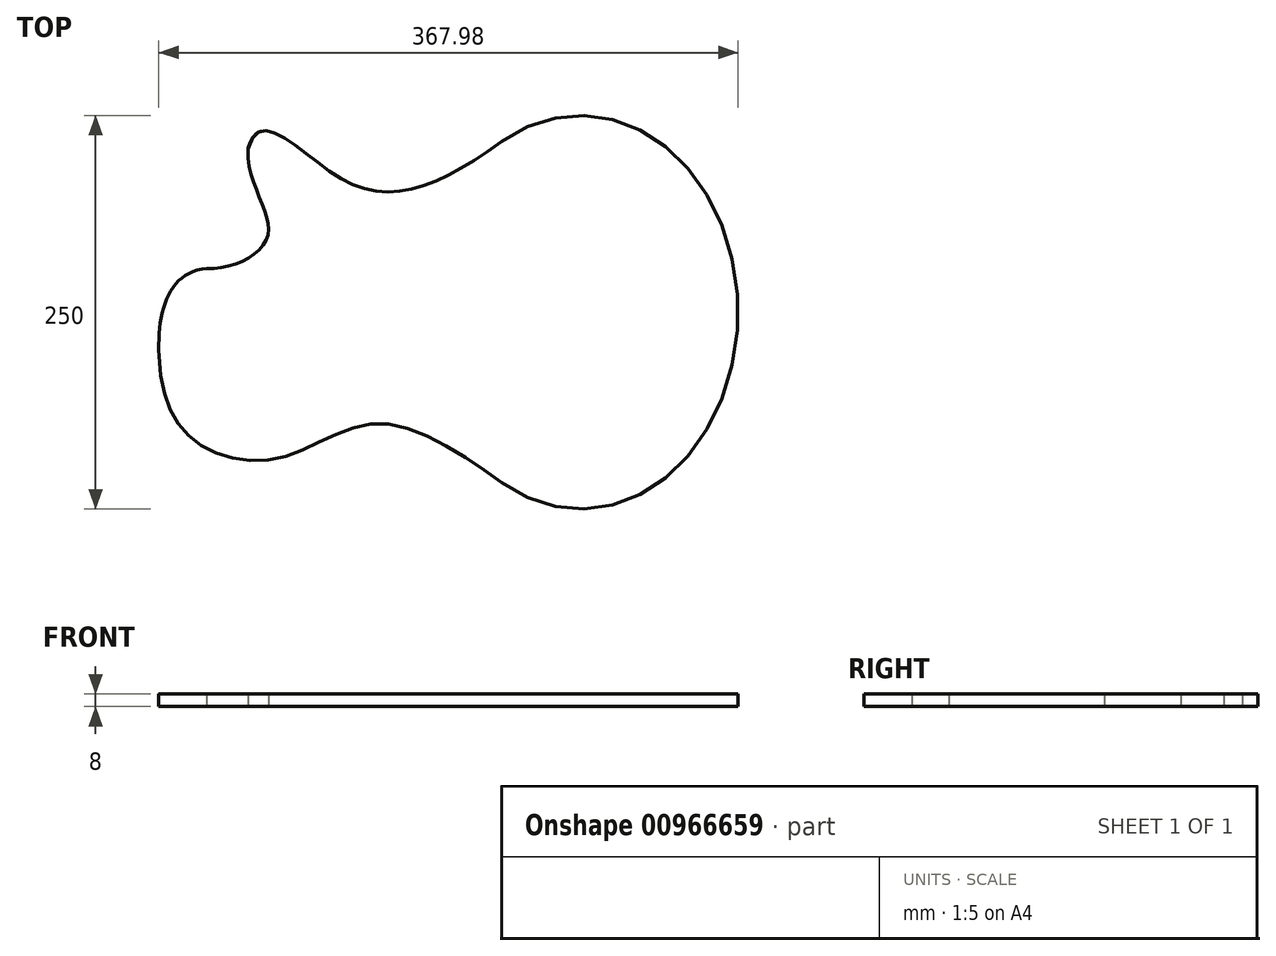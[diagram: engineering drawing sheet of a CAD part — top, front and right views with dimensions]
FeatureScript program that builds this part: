
annotation { "Feature Type Name" : "Feature", "Feature Type Description" : "" }
export const myFeature = defineFeature(function(context is Context, id is Id, definition is map)
    precondition{}
    {
        {
            var Q0;
            Q0=qCreatedBy(makeId("Top.planeOp"),FACE);
            var sketch = newSketch(context, id + "F0", { "sketchPlane" : qUnion([Q0])});
            skLineSegment(sketch, "E0.right", {"start": v(-78.38, 47.9) * mm, "end": v(-78.38, 47.9) * mm});
            skPoint(sketch, "E0.middle", {"position": v(71.81, -15.53) * mm});
            skEllipticalArc(sketch, "E1", {});
            skFitSpline(sketch, "E2", {"points": [v(71.81, 92.78) * mm, v(-30.2, 69.34) * mm, v(-89.37, 87.95) * mm], "startDerivative": vector(-206.74, -148.62) * mm, "endDerivative": vector(-55.75, -204.4) * mm});
            skFitSpline(sketch, "E3", {"points": [v(-89.37, 87.95) * mm, v(-76.74, 32.77) * mm, v(-115.46, 12.22) * mm], "startDerivative": vector(-4.06, -128.91) * mm, "endDerivative": vector(-101.42, 5.56) * mm});
            skFitSpline(sketch, "E4", {"points": [v(71.81, -123.85) * mm, v(-6.94, -86.23) * mm, v(-69.43, -108.17) * mm, v(-124.6, -96.2) * mm, v(-145.88, -43.28) * mm], "startDerivative": vector(-252, 181.15) * mm, "endDerivative": vector(-12.69, 299.13) * mm});
            skFitSpline(sketch, "E5", {"points": [v(-115.46, 12.22) * mm, v(-145.88, -43.28) * mm], "startDerivative": vector(-73.8, -5.98) * mm, "endDerivative": vector(3.53, -83.25) * mm});
            skPoint(sketch, "E6", {"position": v(221.98, -15.53) * mm});
            skFitSpline(sketch, "E7.0", {"points": [v(-81.38, 87.7) * mm, v(-81.45, 85.5) * mm, v(-81.18, 81.15) * mm, v(-79.82, 74.65) * mm, v(-77.72, 68.17) * mm, v(-75.18, 61.7) * mm, v(-72.52, 55.26) * mm, v(-70.5, 49.83) * mm, v(-69.24, 45.36) * mm, v(-68.52, 41.9) * mm, v(-68.2, 38.9) * mm, v(-68.18, 36.45) * mm, v(-68.3, 34.57) * mm, v(-68.5, 32.99) * mm, v(-68.76, 31.72) * mm, v(-69, 30.76) * mm, v(-69.26, 29.82) * mm, v(-69.68, 28.58) * mm, v(-70.29, 27.09) * mm, v(-71.14, 25.37) * mm, v(-72.44, 23.2) * mm, v(-74.3, 20.67) * mm, v(-76.87, 17.93) * mm, v(-80.66, 14.65) * mm, v(-85.96, 11.17) * mm, v(-92.98, 7.91) * mm, v(-100.45, 5.58) * mm, v(-108.16, 4.24) * mm, v(-113.33, 4.09) * mm, v(-115.9, 4.23) * mm]});
            skFitSpline(sketch, "E7.1", {"points": [v(76.48, 86.28) * mm, v(67.74, 80) * mm, v(55.14, 71.52) * mm, v(38.89, 62.74) * mm, v(26.83, 57.6) * mm, v(14.78, 54.1) * mm, v(4.66, 52.8) * mm, v(-3.48, 52.85) * mm, v(-9.58, 53.47) * mm, v(-15.67, 54.68) * mm, v(-21.73, 56.51) * mm, v(-26.74, 58.55) * mm, v(-30.73, 60.49) * mm, v(-33.22, 61.83) * mm, v(-35.2, 62.98) * mm, v(-37.16, 64.17) * mm, v(-39.59, 65.73) * mm, v(-42.45, 67.69) * mm, v(-46.22, 70.38) * mm, v(-50.8, 73.85) * mm, v(-56.1, 78) * mm, v(-61.17, 81.93) * mm, v(-65.91, 85.45) * mm, v(-70.25, 88.37) * mm, v(-73.4, 90.13) * mm, v(-75.5, 91.05) * mm, v(-76.82, 91.5) * mm, v(-77.82, 91.71) * mm, v(-78.46, 91.75) * mm, v(-78.75, 91.71) * mm, v(-78.8, 91.69) * mm, v(-78.85, 91.67) * mm, v(-79.08, 91.5) * mm, v(-79.56, 90.95) * mm, v(-80.2, 89.88) * mm, v(-80.93, 88.22) * mm, v(-81.42, 86.7) * mm, v(-81.66, 85.85) * mm]});
            skFitSpline(sketch, "E7.2", {"points": [v(-114.82, 4.24) * mm, v(-116.02, 4.15) * mm, v(-118.24, 3.81) * mm, v(-121.14, 2.96) * mm, v(-123.68, 1.78) * mm, v(-125.94, 0.3) * mm, v(-127.99, -1.5) * mm, v(-129.86, -3.68) * mm, v(-131.57, -6.23) * mm, v(-133.61, -10.14) * mm, v(-135.68, -15.94) * mm, v(-137.3, -24.13) * mm, v(-138.06, -33.22) * mm, v(-138.02, -39.67) * mm, v(-137.88, -42.94) * mm]});
            skFitSpline(sketch, "E7.3", {"points": [v(76.48, -117.35) * mm, v(71.22, -113.57) * mm, v(62.9, -107.6) * mm, v(51.2, -99.84) * mm, v(42.17, -94.3) * mm, v(32.96, -89.24) * mm, v(23.58, -84.85) * mm, v(15.66, -81.92) * mm, v(9.27, -80.14) * mm, v(4.44, -79.12) * mm, v(-0.41, -78.44) * mm, v(-4.46, -78.2) * mm, v(-7.72, -78.23) * mm, v(-10.93, -78.4) * mm, v(-14.86, -78.86) * mm, v(-19.44, -79.76) * mm, v(-23.88, -80.96) * mm, v(-28.18, -82.38) * mm, v(-33.76, -84.51) * mm, v(-40.47, -87.5) * mm, v(-48.2, -91.24) * mm, v(-54.43, -94.22) * mm, v(-59.3, -96.35) * mm, v(-62.9, -97.8) * mm, v(-66.47, -99.06) * mm, v(-69.4, -99.92) * mm, v(-71.71, -100.5) * mm, v(-74.05, -100.99) * mm, v(-77, -101.46) * mm, v(-80.57, -101.8) * mm, v(-84.15, -101.93) * mm, v(-87.73, -101.83) * mm, v(-92.48, -101.43) * mm, v(-98.3, -100.4) * mm, v(-104.98, -98.4) * mm, v(-110.15, -96.13) * mm, v(-113.97, -94) * mm, v(-116.67, -92.24) * mm, v(-119.18, -90.36) * mm, v(-122.25, -87.67) * mm, v(-125.66, -83.94) * mm, v(-129.14, -78.84) * mm, v(-132.03, -73.07) * mm, v(-134.36, -66.6) * mm, v(-136.72, -57.04) * mm, v(-137.63, -48.83) * mm, v(-137.88, -42.94) * mm]});
            skFitSpline(sketch, "E7.4", {"points": [v(124.05, 101.44) * mm, v(121.81, 101.48) * mm, v(119.57, 101.44) * mm, v(116.6, 101.3) * mm, v(112.89, 100.96) * mm, v(108.48, 100.28) * mm, v(102.65, 99) * mm, v(95.48, 96.76) * mm, v(87.1, 93.02) * mm, v(79.02, 88.25) * mm, v(72.57, 83.44) * mm, v(67.63, 79.1) * mm, v(64.03, 75.6) * mm, v(61.13, 72.49) * mm, v(58.88, 69.88) * mm, v(57.22, 67.86) * mm, v(55.6, 65.79) * mm, v(53.5, 62.97) * mm, v(50.99, 59.32) * mm, v(48.15, 54.78) * mm, v(44.61, 48.5) * mm, v(40.67, 40.27) * mm, v(36.72, 29.86) * mm, v(33.6, 18.99) * mm, v(31.72, 9.62) * mm, v(30.65, 1.99) * mm, v(30.07, -3.8) * mm, v(29.78, -8.67) * mm, v(29.66, -12.59) * mm, v(29.63, -15.53) * mm, v(29.66, -18.48) * mm, v(29.78, -22.4) * mm, v(30.07, -27.26) * mm, v(30.65, -33.05) * mm, v(31.72, -40.69) * mm, v(33.6, -50.06) * mm, v(36.72, -60.92) * mm, v(40.67, -71.34) * mm, v(44.61, -79.57) * mm, v(48.15, -85.85) * mm, v(50.99, -90.4) * mm, v(53.5, -94.03) * mm, v(55.6, -96.86) * mm, v(57.22, -98.93) * mm, v(58.88, -100.95) * mm, v(61.13, -103.56) * mm, v(64.03, -106.67) * mm, v(67.63, -110.17) * mm, v(72.57, -114.5) * mm, v(79.02, -119.32) * mm, v(87.1, -124.08) * mm, v(95.48, -127.82) * mm, v(102.65, -130.07) * mm, v(108.48, -131.34) * mm, v(112.89, -132.03) * mm, v(116.6, -132.37) * mm, v(119.57, -132.51) * mm, v(121.81, -132.54) * mm, v(124.05, -132.51) * mm, v(127.03, -132.37) * mm, v(130.73, -132.03) * mm, v(135.14, -131.34) * mm, v(140.97, -130.07) * mm, v(148.14, -127.82) * mm, v(156.52, -124.08) * mm, v(164.6, -119.32) * mm, v(171.05, -114.5) * mm, v(176, -110.17) * mm, v(179.6, -106.67) * mm, v(182.5, -103.56) * mm, v(184.75, -100.95) * mm, v(186.4, -98.93) * mm, v(188.02, -96.86) * mm, v(190.12, -94.03) * mm, v(192.64, -90.4) * mm, v(195.47, -85.85) * mm, v(199, -79.57) * mm, v(202.95, -71.34) * mm, v(206.9, -60.92) * mm, v(210.02, -50.06) * mm, v(211.9, -40.69) * mm, v(212.97, -33.05) * mm, v(213.55, -27.26) * mm, v(213.84, -22.4) * mm, v(213.96, -18.48) * mm, v(213.99, -15.53) * mm, v(213.96, -12.59) * mm, v(213.84, -8.67) * mm, v(213.55, -3.8) * mm, v(212.97, 1.99) * mm, v(211.9, 9.62) * mm, v(210.02, 18.99) * mm, v(206.9, 29.86) * mm, v(202.95, 40.27) * mm, v(199, 48.5) * mm, v(195.47, 54.78) * mm, v(192.64, 59.32) * mm, v(190.12, 62.97) * mm, v(188.02, 65.79) * mm, v(186.4, 67.86) * mm, v(184.75, 69.88) * mm, v(182.5, 72.49) * mm, v(179.6, 75.6) * mm, v(176, 79.1) * mm, v(171.05, 83.44) * mm, v(164.6, 88.25) * mm, v(156.52, 93.02) * mm, v(148.14, 96.76) * mm, v(140.97, 99) * mm, v(135.14, 100.28) * mm, v(130.73, 100.96) * mm, v(127.03, 101.3) * mm, v(124.05, 101.44) * mm, v(121.81, 101.48) * mm, v(119.57, 101.44) * mm]});
            const initialGuessF0  = {"E1": [0.12181082636041539, -0.01553330506135437, 1, 0, 0.10016679542299138, 0.125, 4.189751328536843, 2.093433978642743]};
            skSetInitialGuess(sketch, initialGuessF0);
            skSolve(sketch);
        }
        {
            var Q0;
            Q0=makeQuery(id+"F0.imprint","IMPRINT",FACE,{"disambiguationData":[TD([[makeQuery(id+"F0.imprint","IMPRINT",EDGE,{"derivedFrom":sQuery(id+"F0.wireOp",EDGE,"E7.0")}),1.0]])]});
            var Q1;
            Q1=makeQuery(id+"F0.imprint","IMPRINT",FACE,{"disambiguationData":[TD([[makeQuery(id+"F0.imprint","IMPRINT",EDGE,{"derivedFrom":sQuery(id+"F0.wireOp",EDGE,"E1")}),1.0]])]});
            extrude(context, id + "F1", {"entities" : qUnion([Q0, Q1]), "depth" : 8 * mm, "offsetDistance" : 25 * mm});
        }
    });
